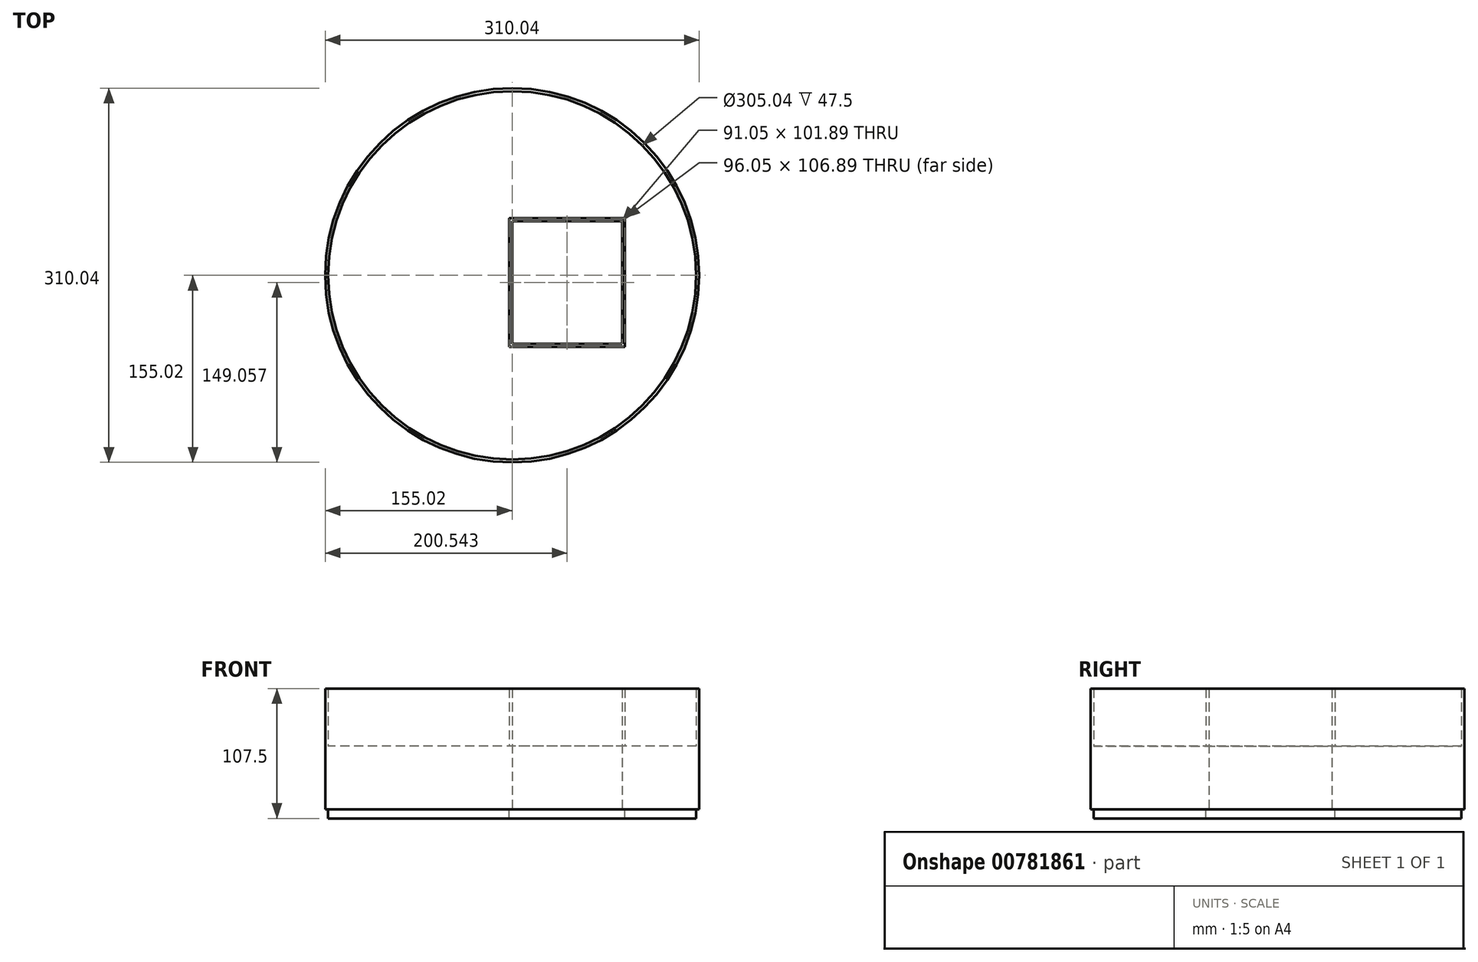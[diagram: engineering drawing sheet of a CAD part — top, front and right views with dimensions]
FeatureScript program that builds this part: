
annotation { "Feature Type Name" : "Feature", "Feature Type Description" : "" }
export const myFeature = defineFeature(function(context is Context, id is Id, definition is map)
    precondition{}
    {
        {
            var Q0;
            Q0=qCreatedBy(makeId("Top.planeOp"),FACE);
            var sketch = newSketch(context, id + "F0", { "sketchPlane" : qUnion([Q0])});
            skCircle(sketch, "E0", {"center": v(0, 0) * mm, "radius": 155.02 * mm});
            skLineSegment(sketch, "E1.bottom", {"start": v(91.05, -56.9) * mm, "end": v(0, -56.9) * mm});
            skLineSegment(sketch, "E1.top", {"start": v(91.05, 44.98) * mm, "end": v(0, 44.98) * mm});
            skLineSegment(sketch, "E1.left", {"start": v(91.05, -56.9) * mm, "end": v(91.05, 44.98) * mm});
            skLineSegment(sketch, "E1.right", {"start": v(0, -56.9) * mm, "end": v(0, 44.98) * mm});
            skSolve(sketch);
        }
        {
            var Q0;
            Q0 = qSketchRegion(id + "F0", true);
            extrude(context, id + "F1", {"entities" : qUnion([Q0]), "depth" : 50 * mm, "offsetDistance" : 25 * mm});
        }
        {
            var Q0;
            Q0=makeQuery(id+"F1.opExtrude","CAP_FACE",FACE,{"disambiguationData":[OSD([sQuery(id+"F0.wireOp",EDGE,"E0")])],"isStart":false});
            shell(context, id + "F2", {"entities" : qUnion([Q0]), "thickness" : 2.5 * mm});
        }
        {
            var Q0;
            Q0 = qSketchRegion(id + "F0", true);
            extrude(context, id + "F3", {"entities" : qUnion([Q0]), "operationType" : NewBodyOperationType.ADD, "oppositeDirection" : true, "depth" : 50 * mm, "offsetDistance" : 25 * mm});
        }
        {
            var Q0;
            {var subQ0=sQuery(id+"F0.wireOp",EDGE,"E1.right");var subQ1=sQuery(id+"F0.wireOp",EDGE,"E1.left");var subQ2=sQuery(id+"F0.wireOp",EDGE,"E1.top");var subQ3=sQuery(id+"F0.wireOp",EDGE,"E1.bottom");var subQ4=sQuery(id+"F0.wireOp",EDGE,"E0");Q0=makeQuery(id+"F2.opShell","OFFSET_FACE",FACE,{"disambiguationData":[OSD([subQ4,subQ3,subQ2,subQ1,subQ0]),TDD([makeQuery(id+"F1.opExtrude","CAP_FACE",FACE,{"disambiguationData":[OSD([subQ4,subQ3,subQ2,subQ1,subQ0])],"isStart":true})])]});}
            extrude(context, id + "F4", {"entities" : qUnion([Q0]), "operationType" : NewBodyOperationType.ADD, "oppositeDirection" : true, "depth" : 60 * mm, "offsetDistance" : 25 * mm});
        }
    });
